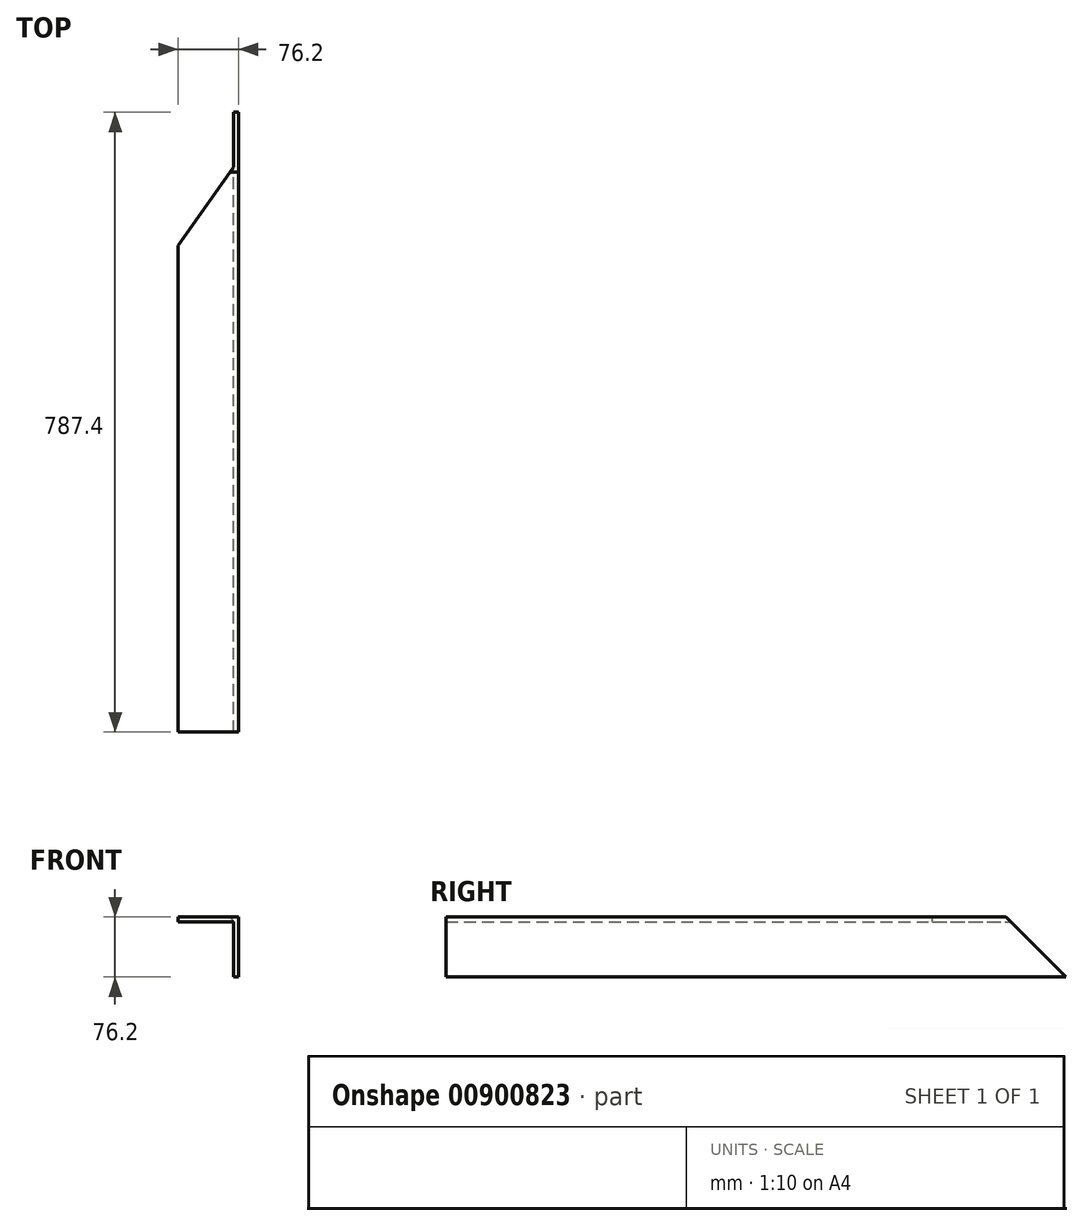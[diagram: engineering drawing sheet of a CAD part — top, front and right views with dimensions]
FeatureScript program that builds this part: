
annotation { "Feature Type Name" : "Feature", "Feature Type Description" : "" }
export const myFeature = defineFeature(function(context is Context, id is Id, definition is map)
    precondition{}
    {
        {
            var Q0;
            Q0=qCreatedBy(makeId("Front.planeOp"),FACE);
            var sketch = newSketch(context, id + "F0", { "sketchPlane" : qUnion([Q0])});
            skLineSegment(sketch, "E0.bottom", {"start": v(38.1, -38.1) * mm, "end": v(31.75, -38.1) * mm});
            skLineSegment(sketch, "E0.top", {"start": v(38.1, 38.1) * mm, "end": v(-38.1, 38.1) * mm});
            skLineSegment(sketch, "E0.left", {"start": v(38.1, -38.1) * mm, "end": v(38.1, 38.1) * mm});
            skLineSegment(sketch, "E0.right", {"start": v(-38.1, 31.75) * mm, "end": v(-38.1, 38.1) * mm});
            skPoint(sketch, "E0.middle", {"position": v(0, 0) * mm});
            skLineSegment(sketch, "E1.0", {"start": v(31.75, 31.75) * mm, "end": v(-38.1, 31.75) * mm});
            skLineSegment(sketch, "E2.0", {"start": v(31.75, -38.1) * mm, "end": v(31.75, 31.75) * mm});
            skPoint(sketch, "E3.orphan", {"position": v(-38.1, -38.1) * mm});
            skSolve(sketch);
        }
        {
            var Q0;
            Q0 = qSketchRegion(id + "F0", true);
            extrude(context, id + "F1", {"entities" : qUnion([Q0]), "depth" : 787.4 * mm, "offsetDistance" : 25.4 * mm});
        }
        {
            var Q0;
            Q0=makeQuery(id+"F1.opExtrude","SWEPT_FACE",FACE,{"disambiguationData":[OSD([sQuery(id+"F0.wireOp",EDGE,"E0.left")])]});
            var sketch = newSketch(context, id + "F2", { "sketchPlane" : qUnion([Q0])});
            skPoint(sketch, "E4.0", {"position": v(0, -38.1) * mm});
            skPoint(sketch, "E5.0", {"position": v(0, 38.1) * mm});
            skLineSegment(sketch, "E6", {"start": v(0, -38.1) * mm, "end": v(-76.2, 38.1) * mm});
            skLineSegment(sketch, "E7", {"start": v(-76.2, 38.1) * mm, "end": v(0, 38.1) * mm});
            skLineSegment(sketch, "E8", {"start": v(0, -38.1) * mm, "end": v(0, 38.1) * mm});
            skSolve(sketch);
        }
        {
            var Q0;
            Q0 = qSketchRegion(id + "F2", true);
            extrude(context, id + "F3", {"entities" : qUnion([Q0]), "operationType" : NewBodyOperationType.REMOVE, "oppositeDirection" : true, "depth" : 76.2 * mm, "offsetDistance" : 25.4 * mm});
        }
        {
            var Q0;
            Q0=makeQuery(id+"F1.opExtrude","SWEPT_FACE",FACE,{"disambiguationData":[OSD([sQuery(id+"F0.wireOp",EDGE,"E0.top")])]});
            var sketch = newSketch(context, id + "F4", { "sketchPlane" : qUnion([Q0])});
            skPoint(sketch, "E9.0", {"position": v(31.75, -69.85) * mm});
            skPoint(sketch, "E10.0", {"position": v(-38.1, -76.2) * mm});
            skPoint(sketch, "E11.0", {"position": v(-38.1, -69.85) * mm});
            skLineSegment(sketch, "E12", {"start": v(31.75, -69.85) * mm, "end": v(-38.1, -169.6) * mm});
            skLineSegment(sketch, "E13", {"start": v(-38.1, -169.6) * mm, "end": v(-38.1, -69.85) * mm});
            skSolve(sketch);
        }
        {
            var Q0;
            {var subQ0=sQuery(id+"F4.wireOp",EDGE,"E13");var subQ1=sQuery(id+"F4.wireOp",EDGE,"E12");var subQ2=sQuery(id+"F0.wireOp",EDGE,"E0.top");var subQ3=makeQuery(id+"F4.imprint","INTERSECT",VERTEX,{"derivedFrom":[makeQuery(id+"F1.opExtrude","SWEPT_EDGE",EDGE,{"disambiguationData":[OSD([subQ2,sQuery(id+"F0.wireOp",EDGE,"E0.right")])]}),subQ1,subQ0]});Q0=makeQuery(id+"F4.imprint","IMPRINT",FACE,{"disambiguationData":[TD([[makeQuery(id+"F4.imprint","IMPRINT",EDGE,{"disambiguationData":[TD([[subQ3,1.0]])],"derivedFrom":subQ1}),-1.0]])]});}
            extrude(context, id + "F5", {"entities" : qUnion([Q0]), "operationType" : NewBodyOperationType.REMOVE, "oppositeDirection" : true, "depth" : 25.4 * mm, "offsetDistance" : 25.4 * mm});
        }
        {
            var Q0;
            Q0=makeQuery(id+"F1.opExtrude","SWEPT_FACE",FACE,{"disambiguationData":[OSD([sQuery(id+"F0.wireOp",EDGE,"E1.0")])]});
            var sketch = newSketch(context, id + "F6", { "sketchPlane" : qUnion([Q0])});
            skPoint(sketch, "E14.0", {"position": v(31.75, 69.85) * mm});
            skPoint(sketch, "E15.0", {"position": v(27.3, 76.2) * mm});
            skPoint(sketch, "E16.0", {"position": v(-38.1, 69.85) * mm});
            skPoint(sketch, "E17.0", {"position": v(-38.1, 76.2) * mm});
            skLineSegment(sketch, "E18", {"start": v(31.75, 69.85) * mm, "end": v(27.3, 76.2) * mm});
            skLineSegment(sketch, "E19", {"start": v(-38.1, 76.2) * mm, "end": v(-38.1, 69.85) * mm});
            skSolve(sketch);
        }
        {
            var Q0;
            Q0=makeQuery(id+"F6.imprint","IMPRINT",FACE,{"disambiguationData":[TD([[makeQuery(id+"F6.imprint","IMPRINT",EDGE,{"derivedFrom":sQuery(id+"F6.wireOp",EDGE,"E19")}),1.0]])]});
            extrude(context, id + "F7", {"entities" : qUnion([Q0]), "operationType" : NewBodyOperationType.REMOVE, "oppositeDirection" : true, "depth" : 25.4 * mm, "offsetDistance" : 25.4 * mm});
        }
    });
